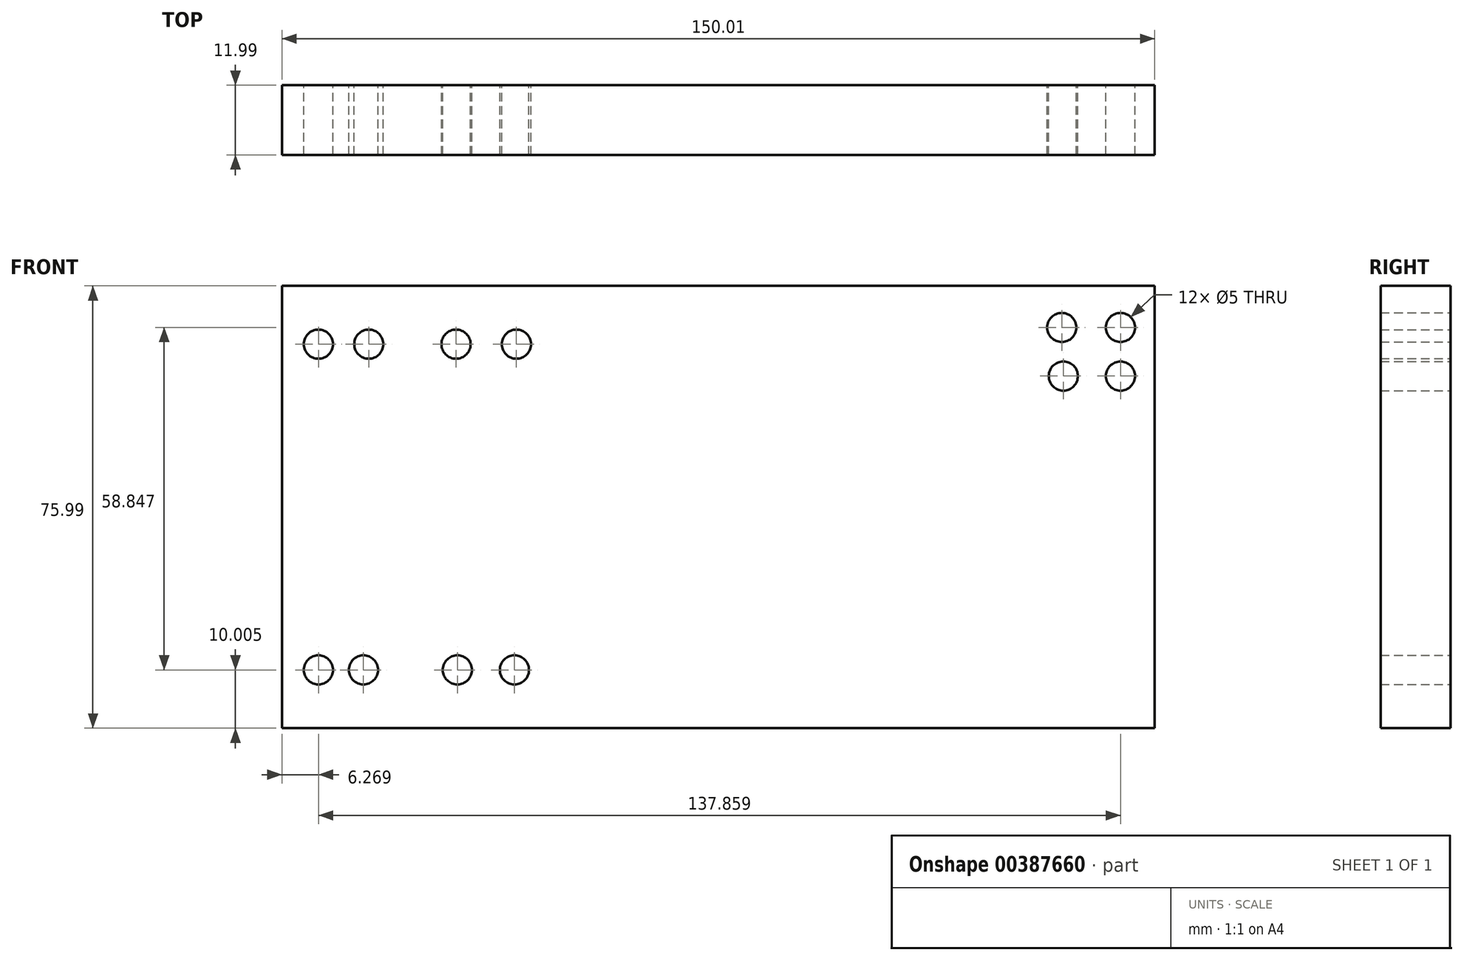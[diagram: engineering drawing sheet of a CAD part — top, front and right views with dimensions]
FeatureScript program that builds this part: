
annotation { "Feature Type Name" : "Feature", "Feature Type Description" : "" }
export const myFeature = defineFeature(function(context is Context, id is Id, definition is map)
    precondition{}
    {
        {
            var Q0;
            Q0=qCreatedBy(makeId("Front.planeOp"),FACE);
            var sketch = newSketch(context, id + "F0", { "sketchPlane" : qUnion([Q0])});
            skLineSegment(sketch, "E0.bottom", {"start": v(-20.68, -17.24) * mm, "end": v(129.33, -17.24) * mm});
            skLineSegment(sketch, "E0.top", {"start": v(-20.68, 58.75) * mm, "end": v(129.33, 58.75) * mm});
            skLineSegment(sketch, "E0.left", {"start": v(-20.68, -17.24) * mm, "end": v(-20.68, 58.75) * mm});
            skLineSegment(sketch, "E0.right", {"start": v(129.33, -17.24) * mm, "end": v(129.33, 58.75) * mm});
            skPoint(sketch, "E1", {"position": v(123.45, 51.61) * mm});
            skPoint(sketch, "E2", {"position": v(123.45, 43.26) * mm});
            skPoint(sketch, "E3", {"position": v(113.63, 43.26) * mm});
            skPoint(sketch, "E4", {"position": v(113.35, 51.61) * mm});
            skCircle(sketch, "E5", {"center": v(113.35, 51.61) * mm, "radius": 2.5 * mm});
            skCircle(sketch, "E6", {"center": v(113.63, 43.26) * mm, "radius": 2.5 * mm});
            skCircle(sketch, "E7", {"center": v(123.45, 43.26) * mm, "radius": 2.5 * mm});
            skCircle(sketch, "E8", {"center": v(123.45, 51.61) * mm, "radius": 2.5 * mm});
            skCircle(sketch, "E9", {"center": v(-14.41, 48.75) * mm, "radius": 2.5 * mm});
            skCircle(sketch, "E10", {"center": v(9.24, 48.75) * mm, "radius": 2.5 * mm});
            skCircle(sketch, "E11", {"center": v(-5.76, 48.75) * mm, "radius": 2.5 * mm});
            skCircle(sketch, "E12", {"center": v(19.62, 48.75) * mm, "radius": 2.5 * mm});
            skCircle(sketch, "E13", {"center": v(-14.41, -7.23) * mm, "radius": 2.5 * mm});
            skCircle(sketch, "E14", {"center": v(-6.68, -7.23) * mm, "radius": 2.5 * mm});
            skCircle(sketch, "E15", {"center": v(9.47, -7.23) * mm, "radius": 2.5 * mm});
            skCircle(sketch, "E16", {"center": v(19.28, -7.23) * mm, "radius": 2.5 * mm});
            skSolve(sketch);
        }
        {
            var Q0;
            Q0=makeQuery(id+"F0.imprint","IMPRINT",FACE,{"disambiguationData":[TD([[makeQuery(id+"F0.imprint","IMPRINT",EDGE,{"derivedFrom":sQuery(id+"F0.wireOp",EDGE,"E0.bottom")}),1.0]])]});
            extrude(context, id + "F1", {"entities" : qUnion([Q0]), "depth" : 12 * mm});
        }
    });
